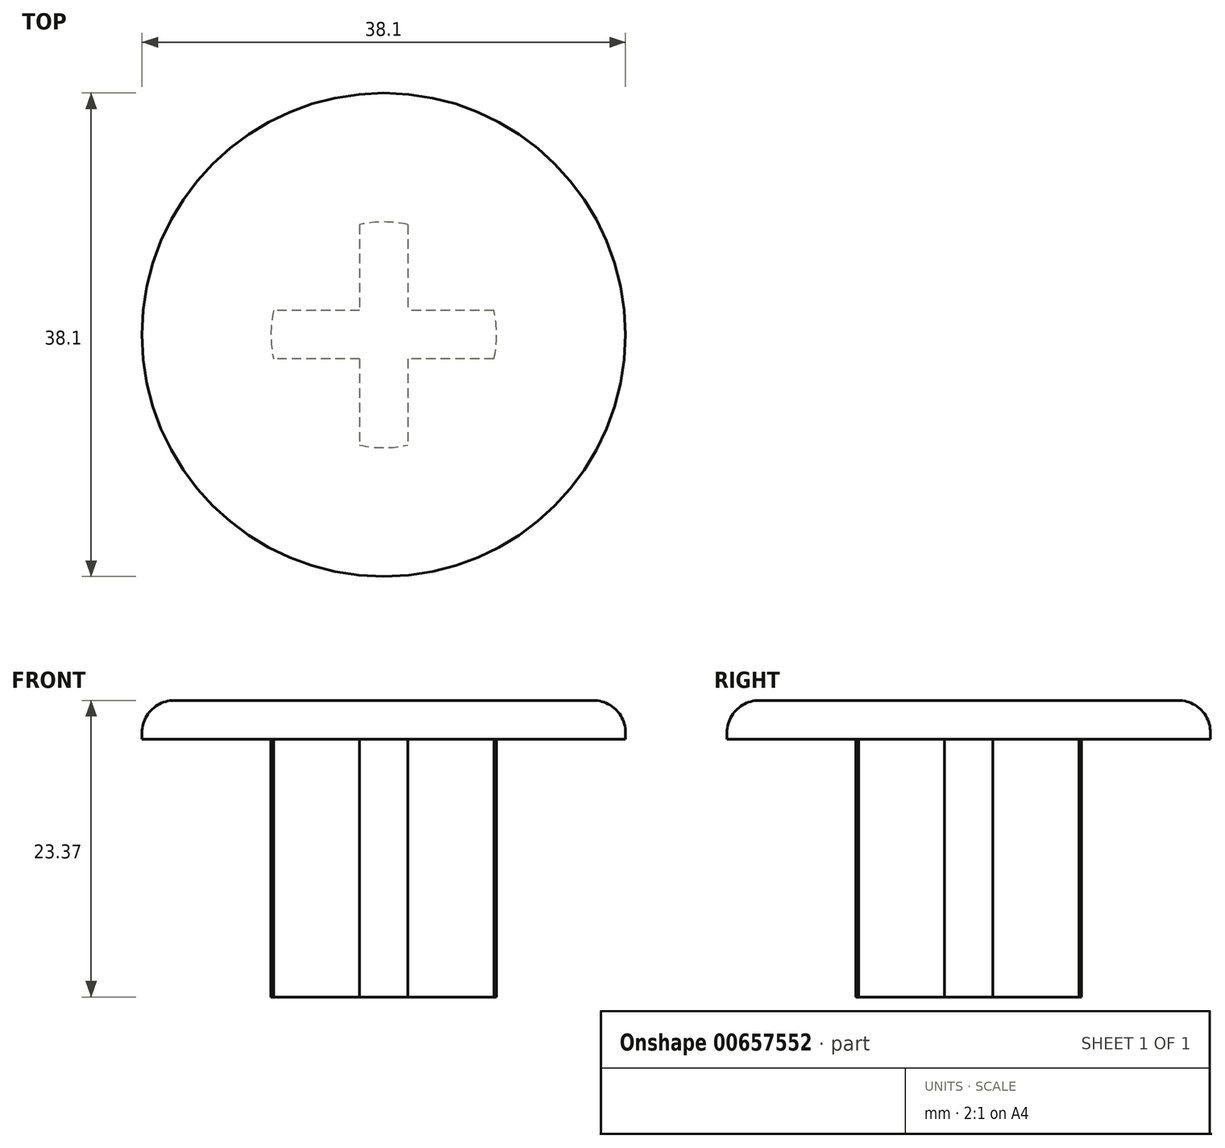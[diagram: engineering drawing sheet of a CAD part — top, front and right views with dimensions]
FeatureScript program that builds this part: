
annotation { "Feature Type Name" : "Feature", "Feature Type Description" : "" }
export const myFeature = defineFeature(function(context is Context, id is Id, definition is map)
    precondition{}
    {
        {
            var Q0;
            Q0=qCreatedBy(makeId("Top.planeOp"),FACE);
            var sketch = newSketch(context, id + "F0", { "sketchPlane" : qUnion([Q0])});
            skCircle(sketch, "E0", {"center": v(0, 0) * mm, "radius": 19.05 * mm});
            skSolve(sketch);
        }
        {
            var Q0;
            Q0 = qSketchRegion(id + "F0", true);
            extrude(context, id + "F1", {"entities" : qUnion([Q0]), "depth" : 3.05 * mm, "offsetDistance" : 25.4 * mm});
        }
        {
            var Q0;
            Q0=makeQuery(id+"F1.opExtrude","CAP_EDGE",EDGE,{"disambiguationData":[OSD([sQuery(id+"F0.wireOp",EDGE,"E0")])],"isStart":false});
            fillet(context, id + "F2", {"entities" : qUnion([Q0]), "radius" : 2.54 * mm, "tangentPropagation" : true, "allowEdgeOverflow" : false});
        }
        {
            var Q0;
            Q0=makeQuery(id+"F1.opExtrude","CAP_FACE",FACE,{"disambiguationData":[OSD([sQuery(id+"F0.wireOp",EDGE,"E0")])],"isStart":true});
            var sketch = newSketch(context, id + "F3", { "sketchPlane" : qUnion([Q0])});
            skLineSegment(sketch, "E1.bottom", {"start": v(8.89, -1.9) * mm, "end": v(-8.9, -1.9) * mm});
            skLineSegment(sketch, "E1.top", {"start": v(8.89, 1.9) * mm, "end": v(-8.9, 1.9) * mm});
            skLineSegment(sketch, "E1.left", {"start": v(8.89, -1.9) * mm, "end": v(8.89, 1.9) * mm});
            skLineSegment(sketch, "E1.right", {"start": v(-8.9, -1.9) * mm, "end": v(-8.9, 1.9) * mm});
            skPoint(sketch, "E1.middle", {"position": v(0, 0) * mm});
            skSolve(sketch);
        }
        {
            var Q0;
            Q0=makeQuery(id+"F3.imprint","IMPRINT",FACE,{"disambiguationData":[TD([[makeQuery(id+"F3.imprint","IMPRINT",EDGE,{"derivedFrom":sQuery(id+"F3.wireOp",EDGE,"E1.bottom")}),1.0]])]});
            var sketch = newSketch(context, id + "F4", { "sketchPlane" : qUnion([Q0])});
            skLineSegment(sketch, "E2.bottom", {"start": v(-1.9, -8.9) * mm, "end": v(1.9, -8.9) * mm});
            skLineSegment(sketch, "E2.top", {"start": v(-1.9, 8.89) * mm, "end": v(1.9, 8.89) * mm});
            skLineSegment(sketch, "E2.left", {"start": v(-1.9, -8.9) * mm, "end": v(-1.9, 8.89) * mm});
            skLineSegment(sketch, "E2.right", {"start": v(1.9, -8.9) * mm, "end": v(1.9, 8.89) * mm});
            skPoint(sketch, "E2.middle", {"position": v(0, 0) * mm});
            skSolve(sketch);
        }
        {
            var Q0;
            Q0=makeQuery(id+"F3.imprint","IMPRINT",FACE,{"disambiguationData":[TD([[makeQuery(id+"F3.imprint","IMPRINT",EDGE,{"derivedFrom":sQuery(id+"F3.wireOp",EDGE,"E1.bottom")}),-1.0]])]});
            var Q1;
            {var subQ0=sQuery(id+"F4.wireOp",EDGE,"E2.bottom");Q1=makeQuery(id+"F4.imprint","IMPRINT",FACE,{"disambiguationData":[TD([[makeQuery(id+"F4.imprint","IMPRINT",EDGE,{"derivedFrom":subQ0}),1.0]])]});}
            var Q2;
            {var subQ0=sQuery(id+"F4.wireOp",EDGE,"E2.top");Q2=makeQuery(id+"F4.imprint","IMPRINT",FACE,{"disambiguationData":[TD([[makeQuery(id+"F4.imprint","IMPRINT",EDGE,{"derivedFrom":subQ0}),-1.0]])]});}
            var Q3;
            {var subQ5=makeQuery(id+"F3.imprint","IMPRINT",EDGE,{"derivedFrom":sQuery(id+"F3.wireOp",EDGE,"E1.right")});Q3=makeQuery(id+"F4.imprint","IMPRINT",FACE,{"disambiguationData":[TD([[makeQuery(id+"F4.imprint","IMPRINT",EDGE,{"derivedFrom":subQ5}),-1.0]])]});}
            var Q4;
            {var subQ5=makeQuery(id+"F3.imprint","IMPRINT",EDGE,{"derivedFrom":sQuery(id+"F3.wireOp",EDGE,"E1.left")});Q4=makeQuery(id+"F4.imprint","IMPRINT",FACE,{"disambiguationData":[TD([[makeQuery(id+"F4.imprint","IMPRINT",EDGE,{"derivedFrom":subQ5}),1.0]])]});}
            var Q5;
            {var subQ0=sQuery(id+"F4.wireOp",EDGE,"E2.left");var subQ1=makeQuery(id+"F3.imprint","IMPRINT",EDGE,{"derivedFrom":sQuery(id+"F3.wireOp",EDGE,"E1.bottom")});var subQ2=makeQuery(id+"F4.imprint","INTERSECT",VERTEX,{"derivedFrom":[subQ1,subQ0]});Q5=makeQuery(id+"F4.imprint","IMPRINT",FACE,{"disambiguationData":[TD([[makeQuery(id+"F4.imprint","IMPRINT",EDGE,{"disambiguationData":[TD([[subQ2,-1.0]])],"derivedFrom":subQ0}),-1.0]])]});}
            extrude(context, id + "F5", {"entities" : qUnion([Q0, Q1, Q2, Q3, Q4, Q5]), "operationType" : NewBodyOperationType.ADD, "depth" : 20.32 * mm, "offsetDistance" : 25.4 * mm});
        }
        {
            var Q0;
            {var subQ0=sQuery(id+"F3.wireOp",EDGE,"E1.right");var subQ1=sQuery(id+"F3.wireOp",EDGE,"E1.left");var subQ2=sQuery(id+"F3.wireOp",EDGE,"E1.top");var subQ3=sQuery(id+"F3.wireOp",EDGE,"E1.bottom");Q0=makeQuery(id+"F5.boolean.opBoolean","MERGE",FACE,{"derivedFrom":[makeQuery(id+"F5.opExtrude","CAP_FACE",FACE,{"disambiguationData":[OSD([subQ3,subQ2,subQ1,subQ0])],"isStart":false}),makeQuery(id+"F5.opExtrude","CAP_FACE",FACE,{"disambiguationData":[OSD([subQ3,subQ2,subQ1,subQ0,sQuery(id+"F4.wireOp",EDGE,"E2.bottom"),sQuery(id+"F4.wireOp",EDGE,"E2.top"),sQuery(id+"F4.wireOp",EDGE,"E2.left"),sQuery(id+"F4.wireOp",EDGE,"E2.right")])],"isStart":false})]});}
            var sketch = newSketch(context, id + "F6", { "sketchPlane" : qUnion([Q0])});
            skCircle(sketch, "E3", {"center": v(0, 0) * mm, "radius": 8.9 * mm});
            skSolve(sketch);
        }
        {
            var Q0;
            {var subQ0=sQuery(id+"F6.wireOp",EDGE,"E3");var subQ2=sQuery(id+"F4.wireOp",EDGE,"E2.top");var subQ5=makeQuery(id+"F5.opExtrude","CAP_EDGE",EDGE,{"disambiguationData":[OSD([subQ2])],"isStart":false});var subQ6=makeQuery(id+"F6.imprint","INTERSECT",VERTEX,{"derivedFrom":[subQ5,subQ0]});Q0=makeQuery(id+"F6.imprint","IMPRINT",FACE,{"disambiguationData":[TD([[makeQuery(id+"F6.imprint","IMPRINT",EDGE,{"disambiguationData":[TD([[subQ6,1.0]])],"derivedFrom":subQ0}),-1.0]])]});}
            extrude(context, id + "F7", {"entities" : qUnion([Q0]), "operationType" : NewBodyOperationType.REMOVE, "oppositeDirection" : true, "depth" : 20.32 * mm, "offsetDistance" : 25.4 * mm});
        }
        {
            var Q0;
            {var subQ0=sQuery(id+"F6.wireOp",EDGE,"E3");var subQ1=sQuery(id+"F4.wireOp",EDGE,"E2.top");var subQ2=makeQuery(id+"F5.opExtrude","CAP_EDGE",EDGE,{"disambiguationData":[OSD([subQ1])],"isStart":false});var subQ3=makeQuery(id+"F6.imprint","INTERSECT",VERTEX,{"derivedFrom":[subQ2,subQ0]});Q0=makeQuery(id+"F6.imprint","IMPRINT",FACE,{"disambiguationData":[TD([[makeQuery(id+"F6.imprint","IMPRINT",EDGE,{"disambiguationData":[TD([[subQ3,-1.0]])],"derivedFrom":subQ0}),-1.0]])]});}
            extrude(context, id + "F8", {"entities" : qUnion([Q0]), "operationType" : NewBodyOperationType.REMOVE, "oppositeDirection" : true, "depth" : 20.32 * mm, "offsetDistance" : 25.4 * mm});
        }
        {
            var Q0;
            {var subQ0=sQuery(id+"F6.wireOp",EDGE,"E3");var subQ1=sQuery(id+"F3.wireOp",EDGE,"E1.right");var subQ2=makeQuery(id+"F3.imprint","IMPRINT",EDGE,{"derivedFrom":subQ1});var subQ3=makeQuery(id+"F5.opExtrude","CAP_EDGE",EDGE,{"disambiguationData":[OSD([subQ1]),TDD([subQ2])],"isStart":false});var subQ4=makeQuery(id+"F6.imprint","INTERSECT",VERTEX,{"derivedFrom":[subQ3,subQ0]});Q0=makeQuery(id+"F6.imprint","IMPRINT",FACE,{"disambiguationData":[TD([[makeQuery(id+"F6.imprint","IMPRINT",EDGE,{"disambiguationData":[TD([[subQ4,-1.0]])],"derivedFrom":subQ0}),-1.0]])]});}
            extrude(context, id + "F9", {"entities" : qUnion([Q0]), "operationType" : NewBodyOperationType.REMOVE, "oppositeDirection" : true, "depth" : 20.32 * mm, "offsetDistance" : 25.4 * mm});
        }
        {
            var Q0;
            {var subQ0=sQuery(id+"F6.wireOp",EDGE,"E3");var subQ1=sQuery(id+"F3.wireOp",EDGE,"E1.right");var subQ2=makeQuery(id+"F3.imprint","IMPRINT",EDGE,{"derivedFrom":subQ1});var subQ11=makeQuery(id+"F5.opExtrude","CAP_EDGE",EDGE,{"disambiguationData":[OSD([subQ1]),TDD([subQ2])],"isStart":false});var subQ12=makeQuery(id+"F6.imprint","INTERSECT",VERTEX,{"derivedFrom":[subQ11,subQ0]});Q0=makeQuery(id+"F6.imprint","IMPRINT",FACE,{"disambiguationData":[TD([[makeQuery(id+"F6.imprint","IMPRINT",EDGE,{"disambiguationData":[TD([[subQ12,1.0]])],"derivedFrom":subQ0}),-1.0]])]});}
            extrude(context, id + "F10", {"entities" : qUnion([Q0]), "operationType" : NewBodyOperationType.REMOVE, "oppositeDirection" : true, "depth" : 20.32 * mm, "offsetDistance" : 25.4 * mm});
        }
        {
            var Q0;
            {var subQ0=sQuery(id+"F6.wireOp",EDGE,"E3");var subQ1=sQuery(id+"F4.wireOp",EDGE,"E2.bottom");var subQ2=makeQuery(id+"F5.opExtrude","CAP_EDGE",EDGE,{"disambiguationData":[OSD([subQ1])],"isStart":false});var subQ3=makeQuery(id+"F6.imprint","INTERSECT",VERTEX,{"derivedFrom":[subQ2,subQ0]});Q0=makeQuery(id+"F6.imprint","IMPRINT",FACE,{"disambiguationData":[TD([[makeQuery(id+"F6.imprint","IMPRINT",EDGE,{"disambiguationData":[TD([[subQ3,-1.0]])],"derivedFrom":subQ0}),-1.0]])]});}
            var Q1;
            {var subQ0=sQuery(id+"F6.wireOp",EDGE,"E3");var subQ2=sQuery(id+"F4.wireOp",EDGE,"E2.bottom");var subQ5=makeQuery(id+"F5.opExtrude","CAP_EDGE",EDGE,{"disambiguationData":[OSD([subQ2])],"isStart":false});var subQ6=makeQuery(id+"F6.imprint","INTERSECT",VERTEX,{"derivedFrom":[subQ5,subQ0]});Q1=makeQuery(id+"F6.imprint","IMPRINT",FACE,{"disambiguationData":[TD([[makeQuery(id+"F6.imprint","IMPRINT",EDGE,{"disambiguationData":[TD([[subQ6,1.0]])],"derivedFrom":subQ0}),-1.0]])]});}
            var Q2;
            {var subQ0=sQuery(id+"F6.wireOp",EDGE,"E3");var subQ1=sQuery(id+"F3.wireOp",EDGE,"E1.left");var subQ2=makeQuery(id+"F3.imprint","IMPRINT",EDGE,{"derivedFrom":subQ1});var subQ3=makeQuery(id+"F5.opExtrude","CAP_EDGE",EDGE,{"disambiguationData":[OSD([subQ1]),TDD([subQ2])],"isStart":false});var subQ4=makeQuery(id+"F6.imprint","INTERSECT",VERTEX,{"derivedFrom":[subQ3,subQ0]});Q2=makeQuery(id+"F6.imprint","IMPRINT",FACE,{"disambiguationData":[TD([[makeQuery(id+"F6.imprint","IMPRINT",EDGE,{"disambiguationData":[TD([[subQ4,1.0]])],"derivedFrom":subQ0}),-1.0]])]});}
            var Q3;
            {var subQ0=sQuery(id+"F6.wireOp",EDGE,"E3");var subQ1=sQuery(id+"F3.wireOp",EDGE,"E1.left");var subQ2=makeQuery(id+"F3.imprint","IMPRINT",EDGE,{"derivedFrom":subQ1});var subQ11=makeQuery(id+"F5.opExtrude","CAP_EDGE",EDGE,{"disambiguationData":[OSD([subQ1]),TDD([subQ2])],"isStart":false});var subQ12=makeQuery(id+"F6.imprint","INTERSECT",VERTEX,{"derivedFrom":[subQ11,subQ0]});Q3=makeQuery(id+"F6.imprint","IMPRINT",FACE,{"disambiguationData":[TD([[makeQuery(id+"F6.imprint","IMPRINT",EDGE,{"disambiguationData":[TD([[subQ12,-1.0]])],"derivedFrom":subQ0}),-1.0]])]});}
            extrude(context, id + "F11", {"entities" : qUnion([Q0, Q1, Q2, Q3]), "operationType" : NewBodyOperationType.REMOVE, "oppositeDirection" : true, "depth" : 20.32 * mm, "offsetDistance" : 25.4 * mm});
        }
    });
